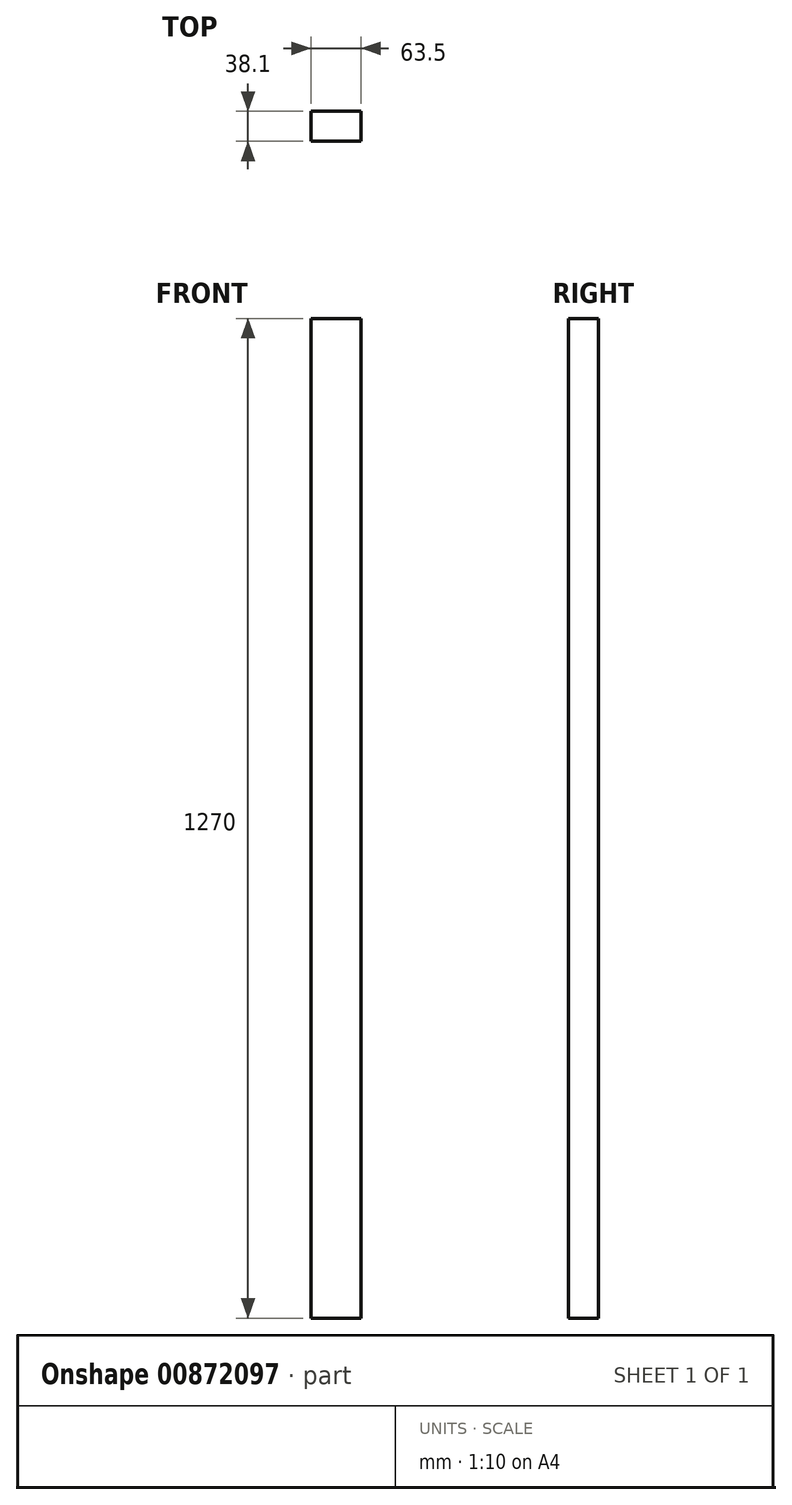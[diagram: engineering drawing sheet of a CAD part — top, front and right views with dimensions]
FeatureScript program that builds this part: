
annotation { "Feature Type Name" : "Feature", "Feature Type Description" : "" }
export const myFeature = defineFeature(function(context is Context, id is Id, definition is map)
    precondition{}
    {
        {
            var Q0;
            Q0=qCreatedBy(makeId("Front.planeOp"),FACE);
            var sketch = newSketch(context, id + "F0", { "sketchPlane" : qUnion([Q0])});
            skLineSegment(sketch, "E0.bottom", {"start": v(-3149.09, -1199.56) * mm, "end": v(-3212.59, -1199.56) * mm});
            skLineSegment(sketch, "E0.top", {"start": v(-3149.09, 70.44) * mm, "end": v(-3212.59, 70.44) * mm});
            skLineSegment(sketch, "E0.left", {"start": v(-3149.09, -1199.56) * mm, "end": v(-3149.09, 70.44) * mm});
            skLineSegment(sketch, "E0.right", {"start": v(-3212.59, -1199.56) * mm, "end": v(-3212.59, 70.44) * mm});
            skPoint(sketch, "E0.middle", {"position": v(-3180.84, -564.56) * mm});
            skSolve(sketch);
        }
        {
            var Q0;
            Q0=qSketchRegion(id+"F0",true);
            extrude(context, id + "F1", {"entities" : qUnion([Q0]), "depth" : 38.1 * mm, "offsetDistance" : 25.4 * mm});
        }
    });
